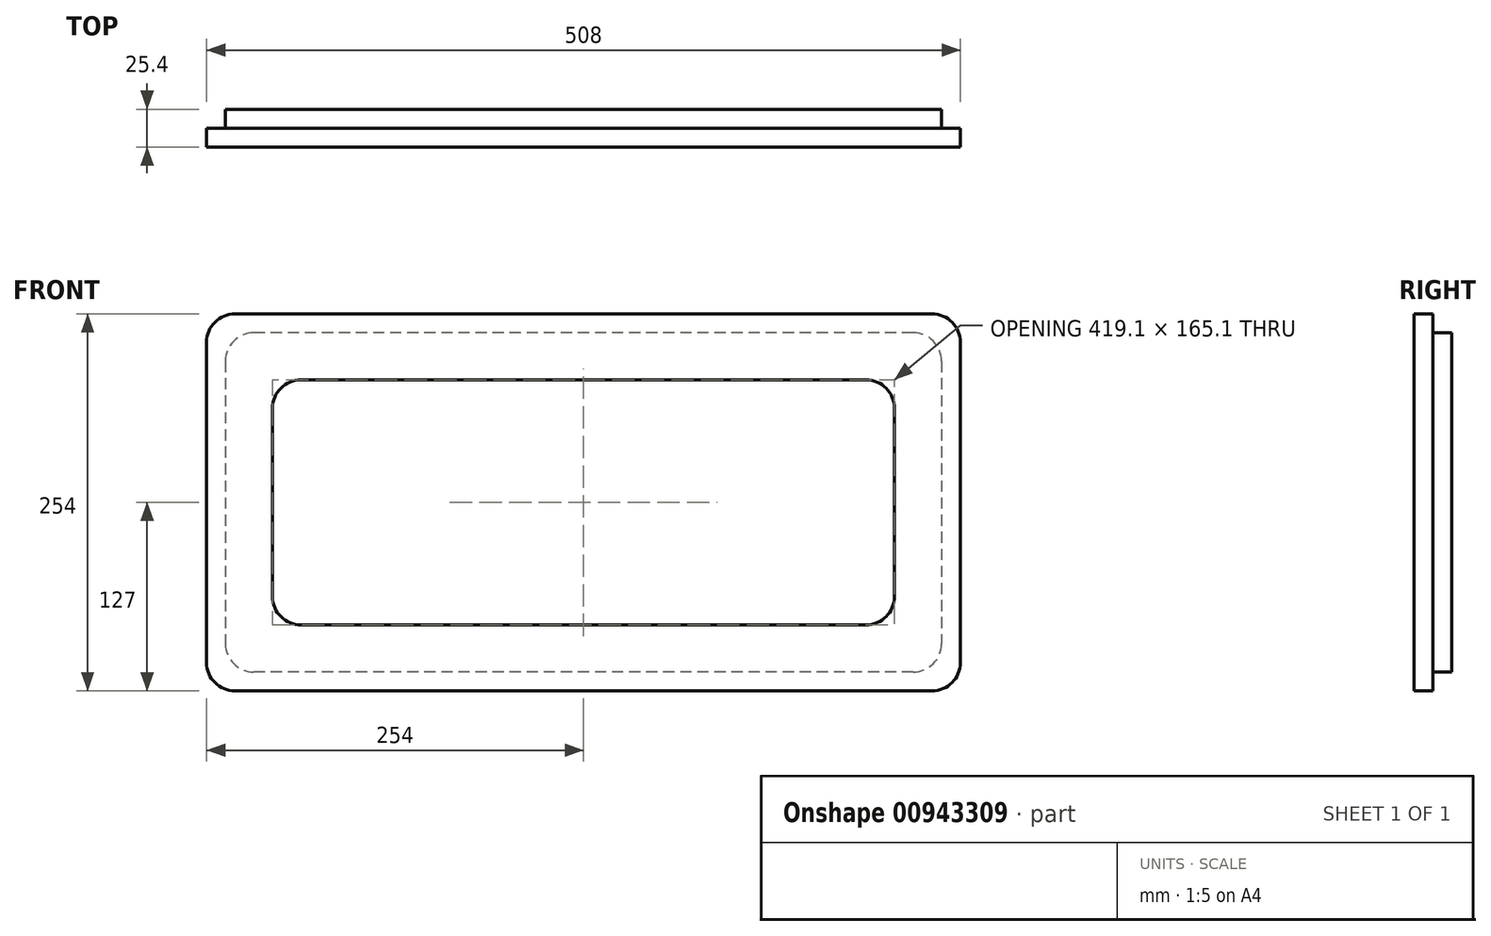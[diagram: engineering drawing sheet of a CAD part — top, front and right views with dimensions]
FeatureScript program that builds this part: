
annotation { "Feature Type Name" : "Feature", "Feature Type Description" : "" }
export const myFeature = defineFeature(function(context is Context, id is Id, definition is map)
    precondition{}
    {
        {
            var Q0;
            Q0=qCreatedBy(makeId("Front.planeOp"),FACE);
            var sketch = newSketch(context, id + "F0", { "sketchPlane" : qUnion([Q0])});
            skLineSegment(sketch, "E0.bottom", {"start": v(-254, 127) * mm, "end": v(254, 127) * mm});
            skLineSegment(sketch, "E0.top", {"start": v(-254, -127) * mm, "end": v(254, -127) * mm});
            skLineSegment(sketch, "E0.left", {"start": v(-254, 127) * mm, "end": v(-254, -127) * mm});
            skLineSegment(sketch, "E0.right", {"start": v(254, 127) * mm, "end": v(254, -127) * mm});
            skLineSegment(sketch, "E1.bottom", {"start": v(-209.55, 82.55) * mm, "end": v(209.55, 82.55) * mm});
            skLineSegment(sketch, "E1.top", {"start": v(-209.55, -82.55) * mm, "end": v(209.55, -82.55) * mm});
            skLineSegment(sketch, "E1.left", {"start": v(-209.55, 82.55) * mm, "end": v(-209.55, -82.55) * mm});
            skLineSegment(sketch, "E1.right", {"start": v(209.55, 82.55) * mm, "end": v(209.55, -82.55) * mm});
            skSolve(sketch);
        }
        {
            var Q0;
            Q0 = qSketchRegion(id + "F0", true);
            extrude(context, id + "F1", {"entities" : qUnion([Q0]), "depth" : 12.7 * mm, "offsetDistance" : 25.4 * mm});
        }
        {
            var Q0;
            Q0=qCreatedBy(makeId("Front.planeOp"),FACE);
            var sketch = newSketch(context, id + "F2", { "sketchPlane" : qUnion([Q0])});
            skLineSegment(sketch, "E2.bottom", {"start": v(241.3, 114.3) * mm, "end": v(-241.3, 114.3) * mm});
            skLineSegment(sketch, "E2.top", {"start": v(241.3, -114.3) * mm, "end": v(-241.3, -114.3) * mm});
            skLineSegment(sketch, "E2.left", {"start": v(241.3, 114.3) * mm, "end": v(241.3, -114.3) * mm});
            skLineSegment(sketch, "E2.right", {"start": v(-241.3, 114.3) * mm, "end": v(-241.3, -114.3) * mm});
            skLineSegment(sketch, "E3.bottom", {"start": v(209.55, 82.55) * mm, "end": v(-209.55, 82.55) * mm});
            skLineSegment(sketch, "E3.top", {"start": v(209.55, -82.55) * mm, "end": v(-209.55, -82.55) * mm});
            skLineSegment(sketch, "E3.left", {"start": v(209.55, 82.55) * mm, "end": v(209.55, -82.55) * mm});
            skLineSegment(sketch, "E3.right", {"start": v(-209.55, 82.55) * mm, "end": v(-209.55, -82.55) * mm});
            skPoint(sketch, "E4.firstSnap0", {"position": v(241.3, 0) * mm});
            skPoint(sketch, "E4.oppositeSnap0", {"position": v(241.3, 0) * mm});
            skSolve(sketch);
        }
        {
            var Q0;
            Q0 = qSketchRegion(id + "F2", true);
            extrude(context, id + "F3", {"entities" : qUnion([Q0]), "operationType" : NewBodyOperationType.ADD, "oppositeDirection" : true, "depth" : 12.7 * mm, "offsetDistance" : 25.4 * mm});
        }
        {
            var Q0;
            Q0=makeQuery(id+"F1.opExtrude","SWEPT_EDGE",EDGE,{"disambiguationData":[OSD([sQuery(id+"F0.wireOp",EDGE,"E0.bottom"),sQuery(id+"F0.wireOp",EDGE,"E0.right")])]});
            var Q1;
            Q1=makeQuery(id+"F3.opExtrude","SWEPT_EDGE",EDGE,{"disambiguationData":[OSD([sQuery(id+"F2.wireOp",EDGE,"E2.bottom"),sQuery(id+"F2.wireOp",EDGE,"E2.left")])]});
            var Q2;
            Q2=makeQuery(id+"F3.opExtrude","SWEPT_EDGE",EDGE,{"disambiguationData":[OSD([sQuery(id+"F2.wireOp",EDGE,"E3.bottom"),sQuery(id+"F2.wireOp",EDGE,"E3.left")])]});
            var Q3;
            Q3=makeQuery(id+"F1.opExtrude","SWEPT_EDGE",EDGE,{"disambiguationData":[OSD([sQuery(id+"F0.wireOp",EDGE,"E0.top"),sQuery(id+"F0.wireOp",EDGE,"E0.right")])]});
            var Q4;
            Q4=makeQuery(id+"F3.opExtrude","SWEPT_EDGE",EDGE,{"disambiguationData":[OSD([sQuery(id+"F2.wireOp",EDGE,"E2.top"),sQuery(id+"F2.wireOp",EDGE,"E2.left")])]});
            var Q5;
            Q5=makeQuery(id+"F3.opExtrude","SWEPT_EDGE",EDGE,{"disambiguationData":[OSD([sQuery(id+"F2.wireOp",EDGE,"E3.top"),sQuery(id+"F2.wireOp",EDGE,"E3.left")])]});
            var Q6;
            Q6=makeQuery(id+"F3.opExtrude","SWEPT_EDGE",EDGE,{"disambiguationData":[OSD([sQuery(id+"F2.wireOp",EDGE,"E3.top"),sQuery(id+"F2.wireOp",EDGE,"E3.right")])]});
            var Q7;
            Q7=makeQuery(id+"F3.opExtrude","SWEPT_EDGE",EDGE,{"disambiguationData":[OSD([sQuery(id+"F2.wireOp",EDGE,"E2.top"),sQuery(id+"F2.wireOp",EDGE,"E2.right")])]});
            var Q8;
            Q8=makeQuery(id+"F1.opExtrude","SWEPT_EDGE",EDGE,{"disambiguationData":[OSD([sQuery(id+"F0.wireOp",EDGE,"E0.top"),sQuery(id+"F0.wireOp",EDGE,"E0.left")])]});
            var Q9;
            Q9=makeQuery(id+"F1.opExtrude","SWEPT_EDGE",EDGE,{"disambiguationData":[OSD([sQuery(id+"F0.wireOp",EDGE,"E0.bottom"),sQuery(id+"F0.wireOp",EDGE,"E0.left")])]});
            var Q10;
            Q10=makeQuery(id+"F3.opExtrude","SWEPT_EDGE",EDGE,{"disambiguationData":[OSD([sQuery(id+"F2.wireOp",EDGE,"E2.bottom"),sQuery(id+"F2.wireOp",EDGE,"E2.right")])]});
            var Q11;
            Q11=makeQuery(id+"F3.opExtrude","SWEPT_EDGE",EDGE,{"disambiguationData":[OSD([sQuery(id+"F2.wireOp",EDGE,"E3.bottom"),sQuery(id+"F2.wireOp",EDGE,"E3.right")])]});
            fillet(context, id + "F4", {"entities" : qUnion([Q0, Q1, Q2, Q3, Q4, Q5, Q6, Q7, Q8, Q9, Q10, Q11]), "radius" : 19.05 * mm, "tangentPropagation" : true, "allowEdgeOverflow" : false});
        }
    });
